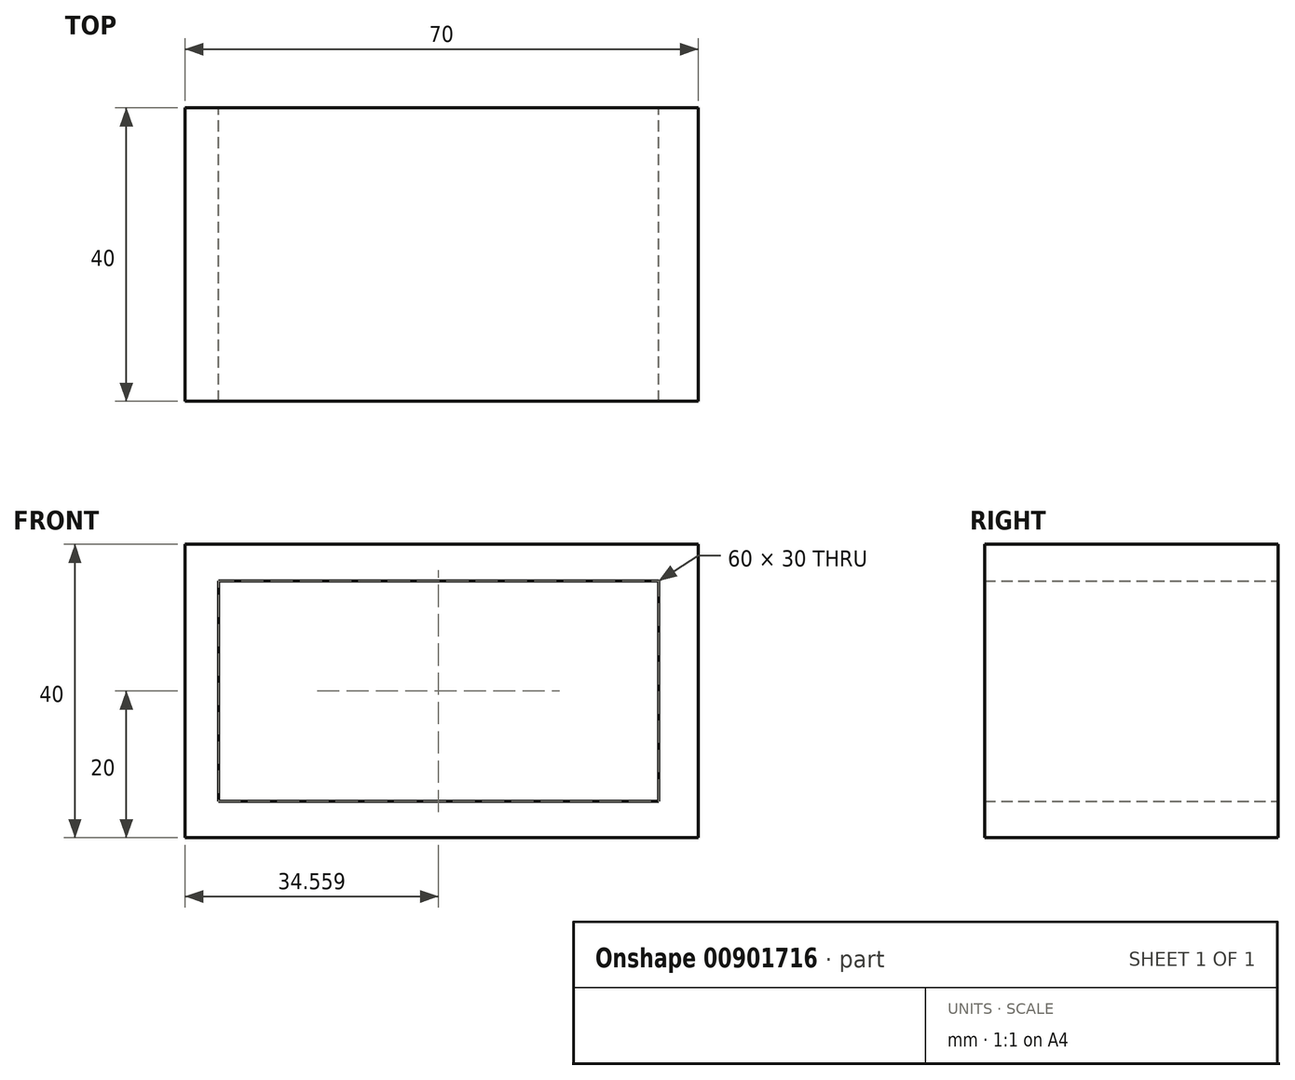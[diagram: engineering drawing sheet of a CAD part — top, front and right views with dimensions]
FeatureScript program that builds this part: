
annotation { "Feature Type Name" : "Feature", "Feature Type Description" : "" }
export const myFeature = defineFeature(function(context is Context, id is Id, definition is map)
    precondition{}
    {
        {
            var Q0;
            Q0=qCreatedBy(makeId("Front.planeOp"),FACE);
            var sketch = newSketch(context, id + "F0", { "sketchPlane" : qUnion([Q0])});
            skLineSegment(sketch, "E0.bottom", {"start": v(0, 0) * mm, "end": v(-70, 0) * mm});
            skLineSegment(sketch, "E0.top", {"start": v(0, 40) * mm, "end": v(-70, 40) * mm});
            skLineSegment(sketch, "E0.left", {"start": v(0, 0) * mm, "end": v(0, 40) * mm});
            skLineSegment(sketch, "E0.right", {"start": v(-70, 0) * mm, "end": v(-70, 40) * mm});
            skLineSegment(sketch, "E1.bottom", {"start": v(-5.44, 5) * mm, "end": v(-65.44, 5) * mm});
            skLineSegment(sketch, "E1.top", {"start": v(-5.44, 35) * mm, "end": v(-65.44, 35) * mm});
            skLineSegment(sketch, "E1.left", {"start": v(-5.44, 5) * mm, "end": v(-5.44, 35) * mm});
            skLineSegment(sketch, "E1.right", {"start": v(-65.44, 5) * mm, "end": v(-65.44, 35) * mm});
            skSolve(sketch);
        }
        {
            var Q0;
            Q0=makeQuery(id+"F0.imprint","IMPRINT",FACE,{"disambiguationData":[TD([[makeQuery(id+"F0.imprint","IMPRINT",EDGE,{"derivedFrom":sQuery(id+"F0.wireOp",EDGE,"E0.bottom")}),-1.0]])]});
            extrude(context, id + "F1", {"entities" : qUnion([Q0]), "depth" : 40 * mm, "offsetDistance" : 25 * mm});
        }
    });
